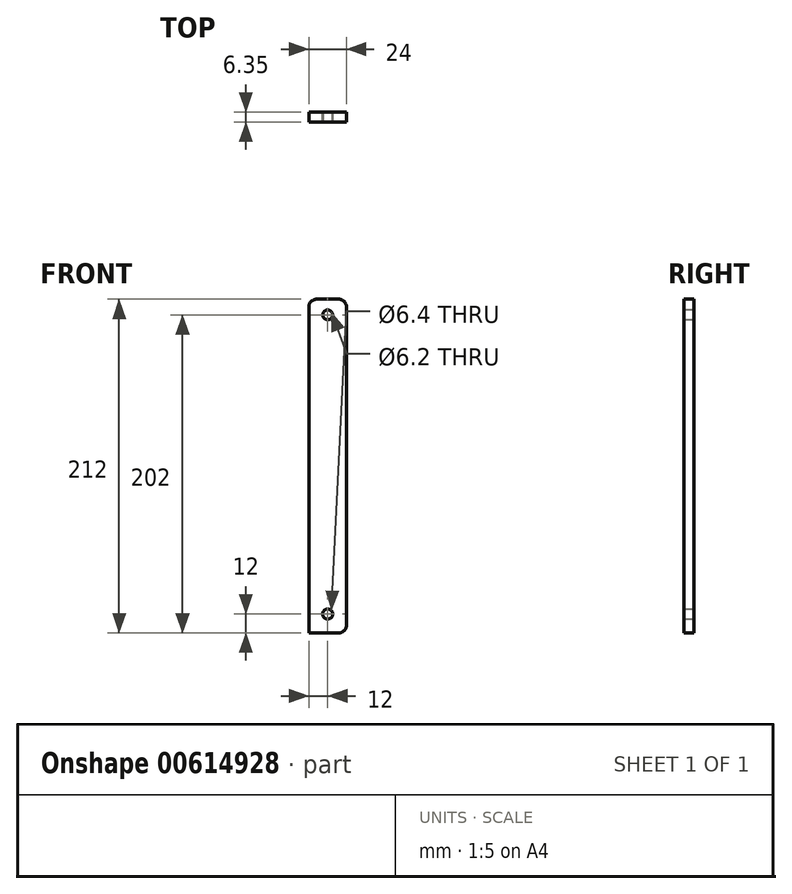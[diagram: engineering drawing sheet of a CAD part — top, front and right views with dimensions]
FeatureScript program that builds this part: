
annotation { "Feature Type Name" : "Feature", "Feature Type Description" : "" }
export const myFeature = defineFeature(function(context is Context, id is Id, definition is map)
    precondition{}
    {
        {
            var Q0;
            Q0=qCreatedBy(makeId("Front.planeOp"),FACE);
            var sketch = newSketch(context, id + "F0", { "sketchPlane" : qUnion([Q0])});
            skCircle(sketch, "E0", {"center": v(0, 0) * mm, "radius": 3.2 * mm});
            skLineSegment(sketch, "E1", {"start": v(0, 0) * mm, "end": v(0, -12) * mm});
            skLineSegment(sketch, "E2", {"start": v(0, -12) * mm, "end": v(0, 0) * mm});
            skLineSegment(sketch, "E3", {"start": v(0, 0) * mm, "end": v(-12, 0) * mm});
            skLineSegment(sketch, "E4", {"start": v(-12, 0) * mm, "end": v(-12, -12) * mm});
            skLineSegment(sketch, "E5", {"start": v(-12, -12) * mm, "end": v(0, -12) * mm});
            skLineSegment(sketch, "E6", {"start": v(0, 0) * mm, "end": v(0, 200) * mm});
            skLineSegment(sketch, "E7", {"start": v(0, 200) * mm, "end": v(-12, 200) * mm});
            skLineSegment(sketch, "E8", {"start": v(-12, 200) * mm, "end": v(0, 200) * mm});
            skLineSegment(sketch, "E9", {"start": v(0, 200) * mm, "end": v(12, 200) * mm});
            skLineSegment(sketch, "E10.bottom", {"start": v(-12, -12) * mm, "end": v(12, -12) * mm});
            skLineSegment(sketch, "E10.top", {"start": v(-12, 200) * mm, "end": v(12, 200) * mm});
            skLineSegment(sketch, "E10.left", {"start": v(-12, -12) * mm, "end": v(-12, 200) * mm});
            skLineSegment(sketch, "E10.right", {"start": v(12, -12) * mm, "end": v(12, 200) * mm});
            skSolve(sketch);
        }
        {
            var Q0;
            {var subQ3=sQuery(id+"F0.wireOp",EDGE,"E0");var subQ7=sQuery(id+"F0.wireOp",EDGE,"E3");var subQ8=makeQuery(id+"F0.imprint","INTERSECT",VERTEX,{"derivedFrom":[subQ3,subQ7]});Q0=makeQuery(id+"F0.imprint","IMPRINT",FACE,{"disambiguationData":[TD([[makeQuery(id+"F0.imprint","IMPRINT",EDGE,{"disambiguationData":[TD([[subQ8,1.0]])],"derivedFrom":subQ3}),-1.0]])]});}
            var Q1;
            {var subQ3=sQuery(id+"F0.wireOp",EDGE,"E10.right");Q1=makeQuery(id+"F0.imprint","IMPRINT",FACE,{"disambiguationData":[TD([[makeQuery(id+"F0.imprint","IMPRINT",EDGE,{"derivedFrom":subQ3}),1.0]])]});}
            var Q2;
            {var subQ5=sQuery(id+"F0.wireOp",EDGE,"E0");var subQ7=sQuery(id+"F0.wireOp",EDGE,"E3");var subQ9=makeQuery(id+"F0.imprint","INTERSECT",VERTEX,{"derivedFrom":[subQ5,subQ7]});Q2=makeQuery(id+"F0.imprint","IMPRINT",FACE,{"disambiguationData":[TD([[makeQuery(id+"F0.imprint","IMPRINT",EDGE,{"disambiguationData":[TD([[subQ9,-1.0]])],"derivedFrom":subQ5}),-1.0]])]});}
            extrude(context, id + "F1", {"entities" : qUnion([Q0, Q1, Q2]), "depth" : 0.12 * 50.8 * mm, "offsetDistance" : 25 * mm});
        }
        {
            var Q0;
            Q0=makeQuery(id+"F1.opExtrude","CAP_FACE",FACE,{"disambiguationData":[OSD([sQuery(id+"F0.wireOp",EDGE,"E0"),sQuery(id+"F0.wireOp",EDGE,"E10.bottom"),sQuery(id+"F0.wireOp",EDGE,"E10.top"),sQuery(id+"F0.wireOp",EDGE,"E10.left"),sQuery(id+"F0.wireOp",EDGE,"E10.right")])],"isStart":false});
            var sketch = newSketch(context, id + "F2", { "sketchPlane" : qUnion([Q0])});
            skLineSegment(sketch, "E11", {"start": v(0, 200) * mm, "end": v(0, 190) * mm});
            skCircle(sketch, "E12", {"center": v(0, 190) * mm, "radius": 3.1 * mm});
            skSolve(sketch);
        }
        {
            var Q0;
            Q0 = qSketchRegion(id + "F2", true);
            extrude(context, id + "F3", {"entities" : qUnion([Q0]), "operationType" : NewBodyOperationType.REMOVE, "oppositeDirection" : true, "depth" : 25 * mm, "offsetDistance" : 25 * mm});
        }
        {
            var Q0;
            Q0=makeQuery(id+"F1.opExtrude","SWEPT_EDGE",EDGE,{"disambiguationData":[OSD([sQuery(id+"F0.wireOp",EDGE,"E10.top"),sQuery(id+"F0.wireOp",EDGE,"E10.right")])]});
            var Q1;
            Q1=makeQuery(id+"F1.opExtrude","SWEPT_EDGE",EDGE,{"disambiguationData":[OSD([sQuery(id+"F0.wireOp",EDGE,"E10.top"),sQuery(id+"F0.wireOp",EDGE,"E10.left")])]});
            var Q2;
            Q2=makeQuery(id+"F1.opExtrude","SWEPT_EDGE",EDGE,{"disambiguationData":[OSD([sQuery(id+"F0.wireOp",EDGE,"E10.bottom"),sQuery(id+"F0.wireOp",EDGE,"E10.right")])]});
            var Q3;
            Q3=makeQuery(id+"F1.opExtrude","SWEPT_EDGE",EDGE,{"disambiguationData":[OSD([sQuery(id+"F0.wireOp",EDGE,"E10.bottom"),sQuery(id+"F0.wireOp",EDGE,"E10.left")])]});
            fillet(context, id + "F4", {"entities" : qUnion([Q0, Q1, Q2, Q3]), "radius" : 5 * mm, "tangentPropagation" : true, "allowEdgeOverflow" : false});
        }
    });
